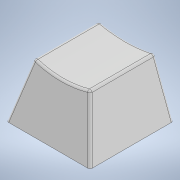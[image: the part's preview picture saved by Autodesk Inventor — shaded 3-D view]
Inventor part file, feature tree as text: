
AUTODESK INVENTOR PART (.ipt)
format: ipt  version: 2022 (Build 260153000, 153)  size: 236,032 bytes
history: native  units: mm
features: sketch x4, other x4, extrude x4, fillet x3, shell x1
ambient origin geometry x8: Origin, YZ Plane, XZ Plane, XY Plane, X Axis, Y Axis, Z Axis, Center Point
bodies: Body1 (feature_tree)
feature tree (16):
  sketch  "スケッチ1"
  other  "作業平面7"
  other  "作業平面9"
  other  "作業平面10"
  other  "作業平面11"
  sketch  "スケッチ10"
  sketch  "スケッチ11"
  extrude  "押し出し2"  Depth=18.0mm
  extrude  "押し出し3"  Depth=18.0mm
  extrude  "押し出し4"  Depth=11.76mm
  shell  "シェル1"  Thickness=12.0mm
  fillet  "フィレット1"  Radius=18.0mm
  fillet  "フィレット2"  Radius=11.0mm
  fillet  "フィレット3"  Radius=14.0mm
  extrude  "押し出し5"  Depth=18.0mm
  sketch  "スケッチ12"
